# Revit family: SDP-859 IP-видеокамера
name_source: partatom
category: Устройства связи
revit_build: Autodesk Revit 2017 (Build: 20170118_1100(x64)
units: mm (PartAtom-declared; Revit-internal decimal feet)

## family parameters
Всегда вертикально = Нет
На основе рабочей плоскости = Нет
Общий = Нет
При загрузке вырезать с полостями = Нет
Размер круглого соединителя = Использовать диаметр
Сохранять ориентацию аннотаций = Нет
Тип детали = Нормальный
Точка расчета площади = Нет

## types (1)
- SDP-859 IP-видеокамера
    ADSK_URL страницы изделия = https://stilsoft.ru
    ADSK_Единица измерения = шт.
    ADSK_Завод-изготовитель = ООО «Основа Безопасности»
    ADSK_Количество = 1
    ADSK_Марка = CТАЕ.426459.032-06
    ADSK_Масса = 0.35
    ADSK_Наименование = IP-видеокамера SDP-859
    ADSK_Размер_Высота = 65 мм
    ADSK_Размер_ДиаметрИзделия = 105 мм
    d_короба = 0 мм
    Дальность ИК = 15
    Максимальное разрешение, пикс = 2048х1536
    Матрица = 1/2,8"CMOS
    Напряжение электропитания видеокамеры = РоЕ (802.3af)
    Поддерживаемые протоколы = RTP/RTSP/RTCP, TCP/UDP, HTTP, DHCP, PPPoE, DNS, DDNS, PPPoE, SMTP, NTP, IPv4/IPv6, Banjour
    Потребляемый ток, не более, А = 0 А
    Тип интерфейса = 1 разъем RJ45 10M/100M Ethernet порт
    Управление = Веб-интерфейс, StilVL
    Фокусное расстояние объектива, мм = 4 мм
    Формат сжатия = H.264, MJPEG
    Частота кадров, к/сек = 25
    Чувствительность Цвет, Люкс = 0,02 / F1.4
    Чувствительность Ч/б, Люкс = 0,001 / F1.4
    Чувствительность с вкл. ИК, Люкс = 0
